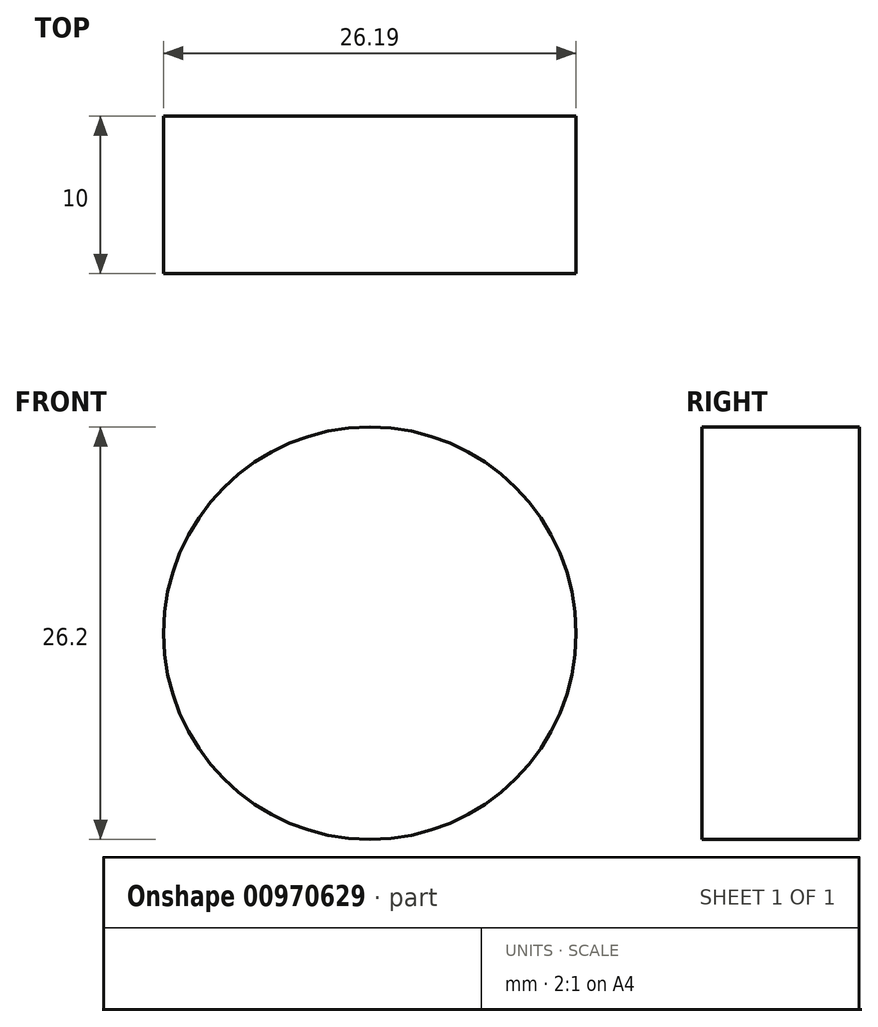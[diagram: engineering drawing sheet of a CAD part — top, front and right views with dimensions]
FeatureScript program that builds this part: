
annotation { "Feature Type Name" : "Feature", "Feature Type Description" : "" }
export const myFeature = defineFeature(function(context is Context, id is Id, definition is map)
    precondition{}
    {
        {
            var Q0;
            Q0=qCreatedBy(makeId("Front.planeOp"),FACE);
            var sketch = newSketch(context, id + "F0", { "sketchPlane" : qUnion([Q0])});
            skCircle(sketch, "E0", {"center": v(-57.12, 45) * mm, "radius": 13.1 * mm});
            skSolve(sketch);
        }
        {
            var Q0;
            Q0 = qSketchRegion(id + "F0", true);
            extrude(context, id + "F1", {"entities" : qUnion([Q0]), "depth" : 10 * mm, "offsetDistance" : 25 * mm});
        }
    });
